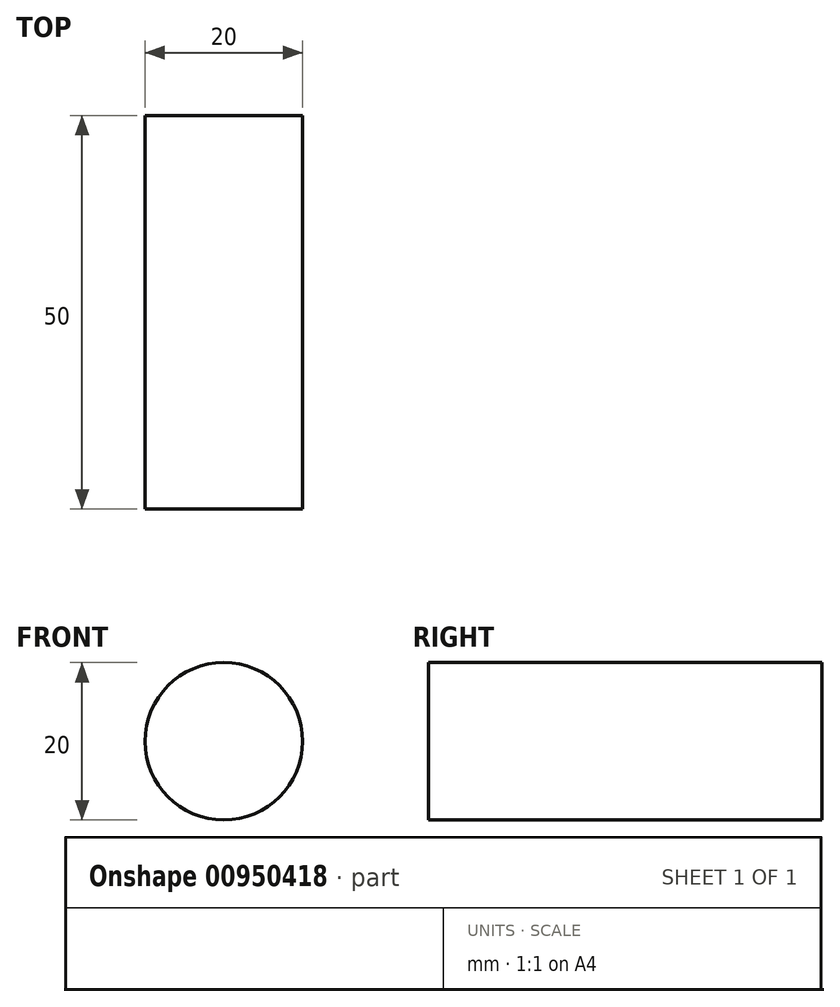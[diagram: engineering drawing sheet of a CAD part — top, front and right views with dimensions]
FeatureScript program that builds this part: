
annotation { "Feature Type Name" : "Feature", "Feature Type Description" : "" }
export const myFeature = defineFeature(function(context is Context, id is Id, definition is map)
    precondition{}
    {
        {
            var Q0;
            Q0=qCreatedBy(makeId("Front.planeOp"),FACE);
            var sketch = newSketch(context, id + "F0", { "sketchPlane" : qUnion([Q0])});
            skCircle(sketch, "E0", {"center": v(0, 0) * mm, "radius": 10 * mm});
            skSolve(sketch);
        }
        {
            var Q0;
            Q0 = qSketchRegion(id + "F0", true);
            extrude(context, id + "F1", {"entities" : qUnion([Q0]), "depth" : 50 * mm, "offsetDistance" : 25.4 * mm});
        }
    });
